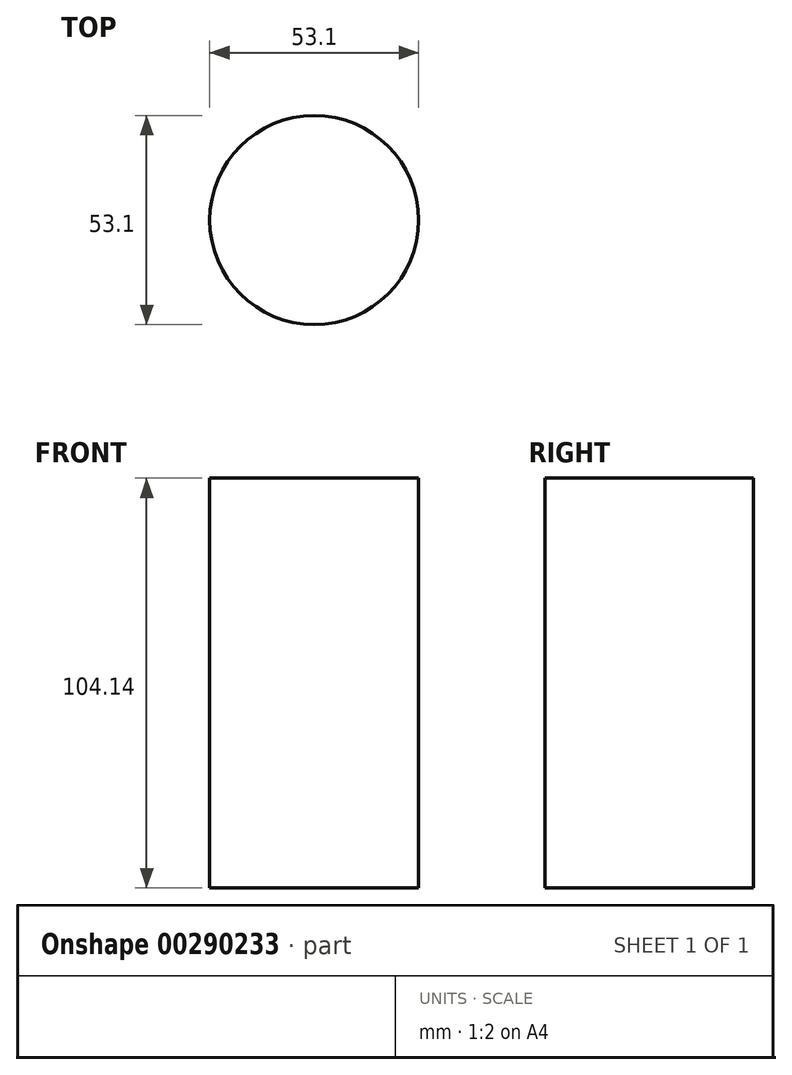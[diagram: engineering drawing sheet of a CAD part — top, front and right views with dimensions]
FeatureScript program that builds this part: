
annotation { "Feature Type Name" : "Feature", "Feature Type Description" : "" }
export const myFeature = defineFeature(function(context is Context, id is Id, definition is map)
    precondition{}
    {
        {
            var Q0;
            Q0=qCreatedBy(makeId("Top.planeOp"),FACE);
            var sketch = newSketch(context, id + "F0", { "sketchPlane" : qUnion([Q0])});
            skCircle(sketch, "E0", {"center": v(0, 0) * mm, "radius": 26.55 * mm});
            skSolve(sketch);
        }
        {
            var Q0;
            Q0=makeQuery(id+"F0.imprint","IMPRINT",FACE,{"disambiguationData":[TD([[makeQuery(id+"F0.imprint","IMPRINT",EDGE,{"derivedFrom":sQuery(id+"F0.wireOp",EDGE,"E0")}),1.0]])]});
            var Q1;
            Q1 = qConstructionFilter(qBodyType(qCreatedBy(id + "F0" ,EDGE), BodyType.WIRE), ConstructionObject.NO);
            extrude(context, id + "F1", {"entities" : qUnion([Q0]), "surfaceEntities" : qUnion([Q1]), "endBound" : BoundingType.SYMMETRIC, "depth" : 104.14 * mm});
        }
    });
